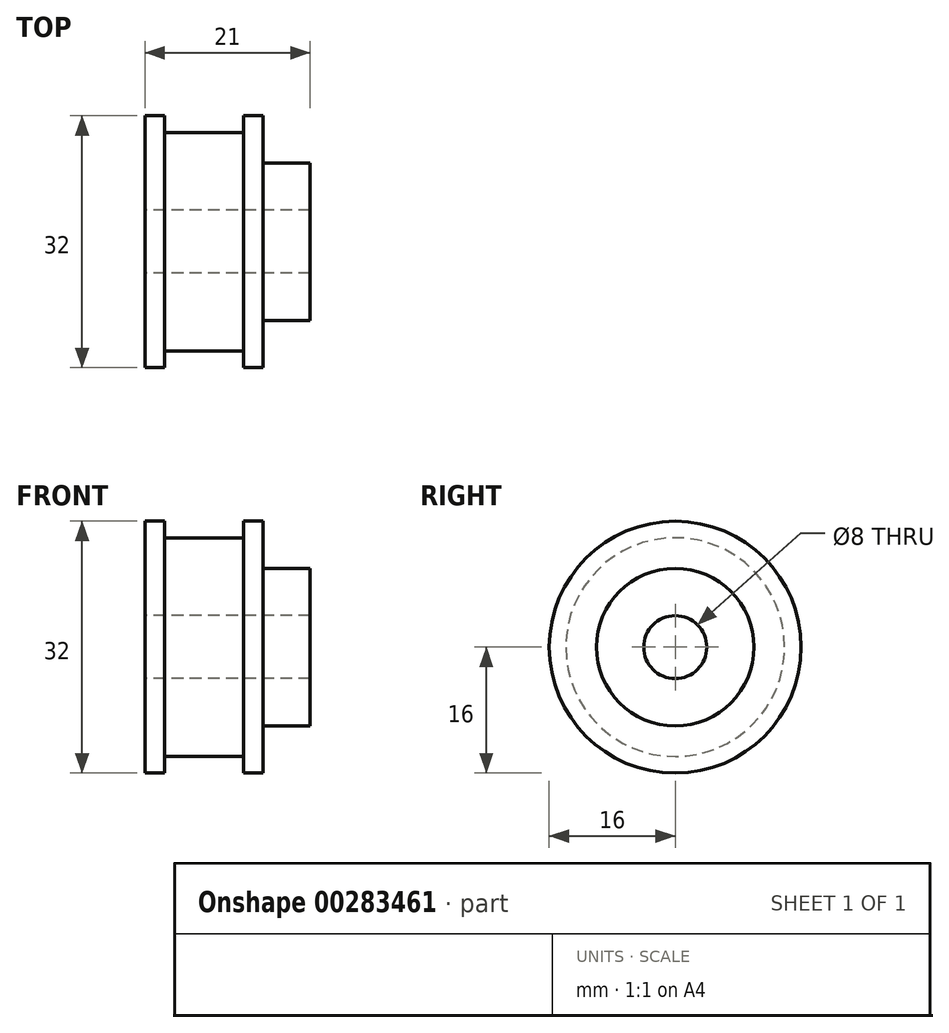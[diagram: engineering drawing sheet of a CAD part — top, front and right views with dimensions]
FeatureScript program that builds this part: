
annotation { "Feature Type Name" : "Feature", "Feature Type Description" : "" }
export const myFeature = defineFeature(function(context is Context, id is Id, definition is map)
    precondition{}
    {
        {
            var Q0;
            Q0=qCreatedBy(makeId("Front.planeOp"),FACE);
            var sketch = newSketch(context, id + "F0", { "sketchPlane" : qUnion([Q0])});
            skLineSegment(sketch, "E0", {"start": v(-18.22, 0) * mm, "end": v(20.5, 0) * mm, "construction": true});
            skLineSegment(sketch, "E1", {"start": v(6, 4) * mm, "end": v(-15, 4) * mm});
            skLineSegment(sketch, "E2", {"start": v(-15, 4) * mm, "end": v(-15, 16) * mm});
            skLineSegment(sketch, "E3", {"start": v(-15, 16) * mm, "end": v(-12.5, 16) * mm});
            skLineSegment(sketch, "E4", {"start": v(-12.5, 16) * mm, "end": v(-12.5, 13.9) * mm});
            skLineSegment(sketch, "E5", {"start": v(-12.5, 13.9) * mm, "end": v(-2.5, 13.9) * mm});
            skLineSegment(sketch, "E6", {"start": v(-2.5, 13.9) * mm, "end": v(-2.5, 16) * mm});
            skLineSegment(sketch, "E7", {"start": v(-2.5, 16) * mm, "end": v(0, 16) * mm});
            skLineSegment(sketch, "E8", {"start": v(0, 16) * mm, "end": v(0, 10) * mm});
            skLineSegment(sketch, "E9", {"start": v(0, 10) * mm, "end": v(6, 10) * mm});
            skLineSegment(sketch, "E10", {"start": v(6, 10) * mm, "end": v(6, 4) * mm});
            skSolve(sketch);
        }
        {
            var Q0;
            Q0=qSketchRegion(id+"F0",true);
            var Q1;
            Q1=sQuery(id+"F0.wireOp",EDGE,"E0");
            revolve(context, id + "F1", {"entities" : qUnion([Q0]), "axis" : qUnion([Q1]), "revolveType" : RevolveType.FULL});
        }
    });
